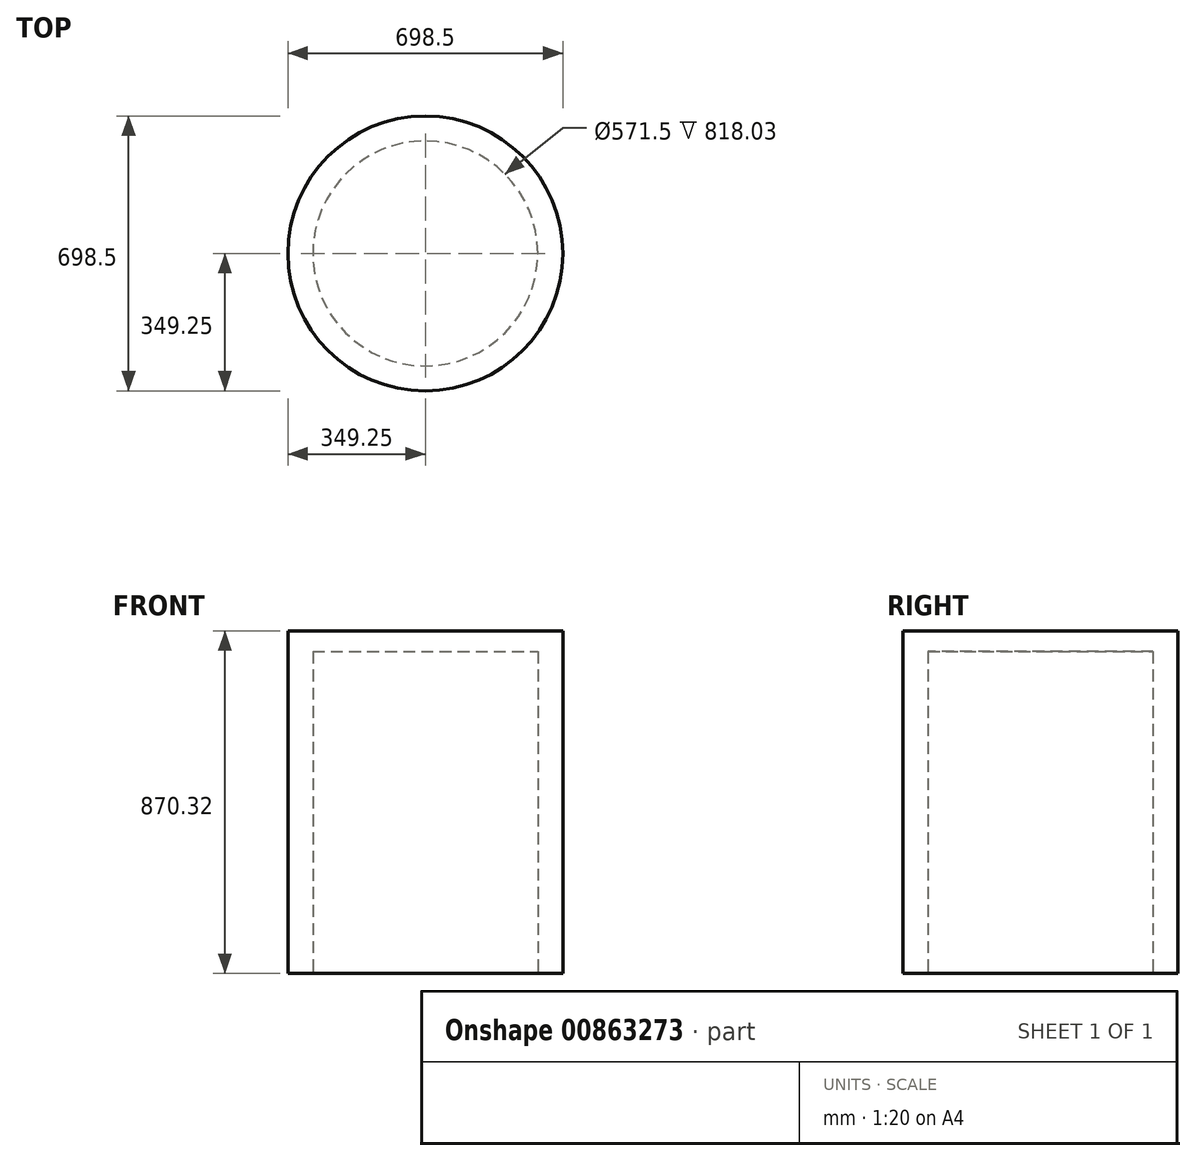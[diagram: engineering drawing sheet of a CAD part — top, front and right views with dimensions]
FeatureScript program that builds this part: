
annotation { "Feature Type Name" : "Feature", "Feature Type Description" : "" }
export const myFeature = defineFeature(function(context is Context, id is Id, definition is map)
    precondition{}
    {
        {
            var Q0;
            Q0=qCreatedBy(makeId("Front.planeOp"),FACE);
            var sketch = newSketch(context, id + "F0", { "sketchPlane" : qUnion([Q0])});
            skLineSegment(sketch, "E0", {"start": v(0, 0) * mm, "end": v(0, 870.32) * mm});
            skLineSegment(sketch, "E1", {"start": v(0, 870.32) * mm, "end": v(349.25, 870.32) * mm});
            skLineSegment(sketch, "E2", {"start": v(349.25, 870.32) * mm, "end": v(349.25, 0) * mm});
            skLineSegment(sketch, "E3", {"start": v(349.25, 0) * mm, "end": v(285.75, 0) * mm});
            skLineSegment(sketch, "E4", {"start": v(285.75, 0) * mm, "end": v(285.75, 818.03) * mm});
            skLineSegment(sketch, "E5", {"start": v(285.75, 818.03) * mm, "end": v(0, 818.03) * mm});
            skSolve(sketch);
        }
        {
            var Q0;
            {var subQ0=sQuery(id+"F0.wireOp",EDGE,"E1");Q0=makeQuery(id+"F0.imprint","IMPRINT",FACE,{"disambiguationData":[TD([[makeQuery(id+"F0.imprint","IMPRINT",EDGE,{"derivedFrom":subQ0}),-1.0]])]});}
            var Q1;
            Q1=sQuery(id+"F0.wireOp",EDGE,"E0");
            revolve(context, id + "F1", {"surfaceOperationType" : NewSurfaceOperationType.NEW, "entities" : qUnion([Q0]), "axis" : qUnion([Q1]), "revolveType" : RevolveType.FULL});
        }
    });
